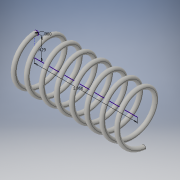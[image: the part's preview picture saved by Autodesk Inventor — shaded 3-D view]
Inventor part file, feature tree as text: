
AUTODESK INVENTOR PART (.ipt)
format: ipt  version: 2016 (Build 200138000, 138)  size: 386,560 bytes
history: native  units: in
note: dims shown in document units (in); Inventor stores cm internally (conversion verified against a paired STEP export)
features: helix x1, sketch x1
ambient origin geometry x8: Origin, YZ Plane, XZ Plane, XY Plane, X Axis, Y Axis, Z Axis, Center Point
bodies: Solid1 (feature_tree)
feature tree (2):
  helix  "Coil1"  [1 undecoded]
  sketch  "Sketch1"  dims[d1=0.08in d2=0.429in d3=1.0in d4=1.95in d5=2.7559in d6=0.0in d7=90.0deg d8=90.0deg d9=0.0in d10=0.0in]
note: 1 required parameter value undecoded (feature->parameter linkage not recoverable at this tier; creation-order binding heuristic only, values carry confidence <= 0.55)
